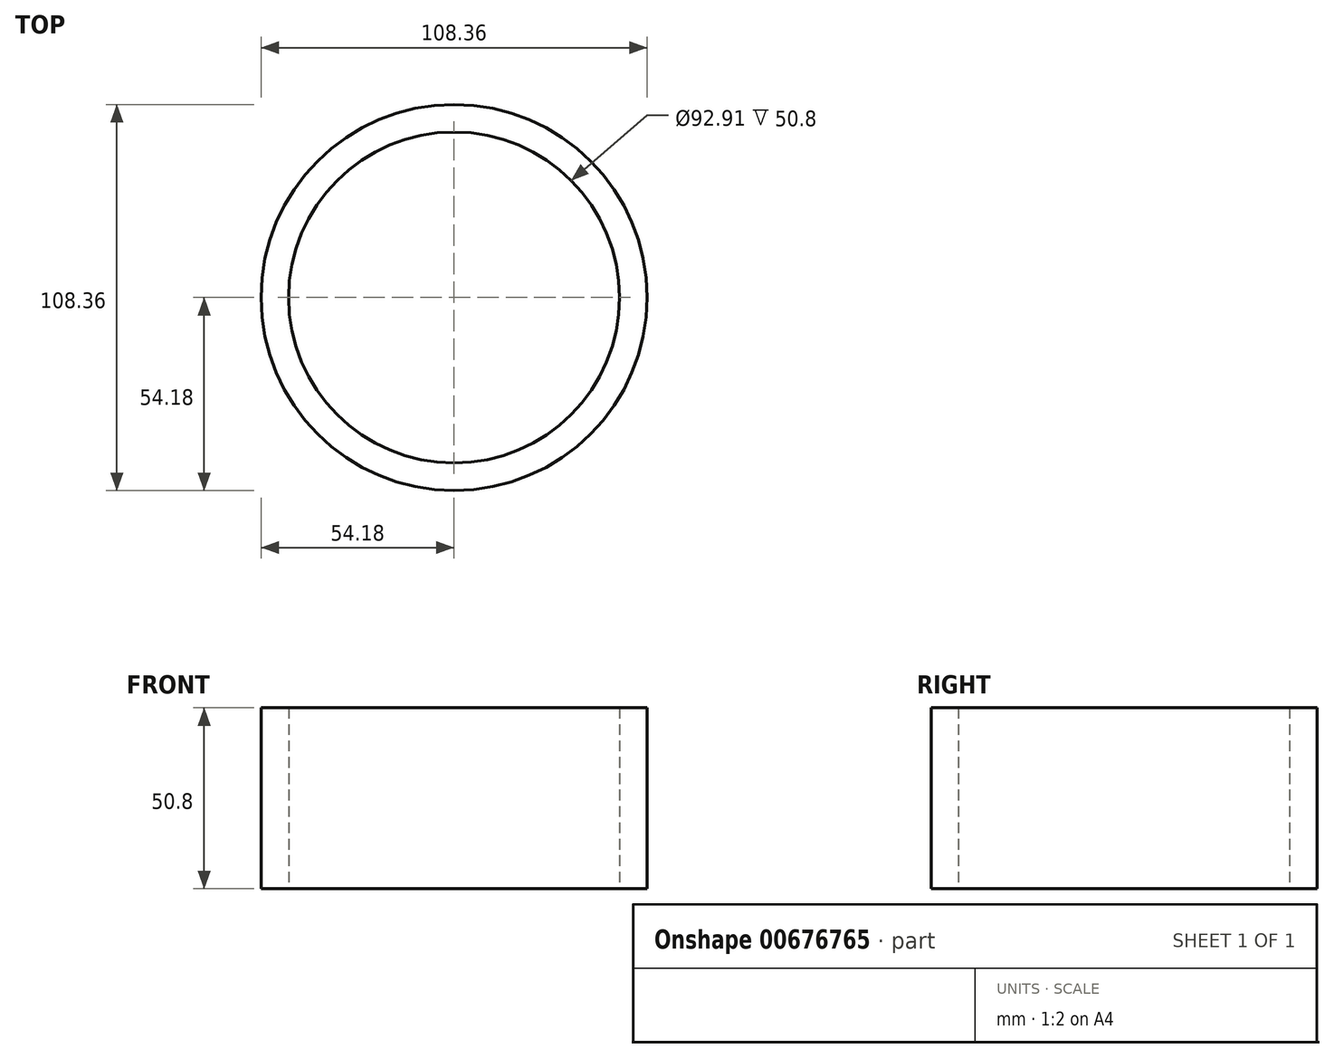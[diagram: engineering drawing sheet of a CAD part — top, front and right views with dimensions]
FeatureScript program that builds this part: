
annotation { "Feature Type Name" : "Feature", "Feature Type Description" : "" }
export const myFeature = defineFeature(function(context is Context, id is Id, definition is map)
    precondition{}
    {
        {
            var Q0;
            Q0=qCreatedBy(makeId("Top.planeOp"),FACE);
            var sketch = newSketch(context, id + "F0", { "sketchPlane" : qUnion([Q0])});
            skCircle(sketch, "E0", {"center": v(0, 0) * mm, "radius": 46.46 * mm});
            skCircle(sketch, "E1", {"center": v(0, 0) * mm, "radius": 54.18 * mm});
            skSolve(sketch);
        }
        {
            var Q0;
            Q0 = qSketchRegion(id + "F0", true);
            extrude(context, id + "F1", {"entities" : qUnion([Q0]), "depth" : 50.8 * mm, "offsetDistance" : 25.4 * mm});
        }
        {
            var Q0;
            Q0=qCreatedBy(makeId("Top.planeOp"),FACE);
            var sketch = newSketch(context, id + "F2", { "sketchPlane" : qUnion([Q0])});
            skCircle(sketch, "E2.0", {"center": v(0, 0) * mm, "radius": 54.18 * mm});
            skLineSegment(sketch, "E3", {"start": v(0, 0) * mm, "end": v(46.92, 27.1) * mm});
            skLineSegment(sketch, "E4", {"start": v(0, 0) * mm, "end": v(54.18, 0) * mm});
            skSolve(sketch);
        }
    });
